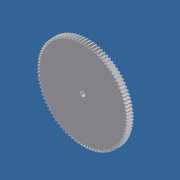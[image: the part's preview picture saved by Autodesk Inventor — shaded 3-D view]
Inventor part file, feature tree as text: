
AUTODESK INVENTOR PART (.ipt)
format: ipt  version: unknown  size: 956,928 bytes
history: native  units: in
note: dims shown in document units (in); Inventor stores cm internally (conversion verified against a paired STEP export)
features: extrude x3, sketch x3, imported_body x1
ambient origin geometry x8: Origin, YZ Plane, XZ Plane, XY Plane, X Axis, Y Axis, Z Axis, Center Point
bodies: Solid1 (feature_tree)
feature tree (7):
  imported_body  "Base1"
  extrude  "Extrusion2"  Depth=0.66in TaperAngle=0.0deg
  extrude  "Extrusion3"  Depth=0.41in TaperAngle=0.0deg
  extrude  "Extrusion4"  Depth=0.171in
  sketch  "Sketch2"  dims[d6=0.215in d7=0.66in d8=0.0in]
  sketch  "Sketch3"  dims[d9=0.7in d11=0.41in d12=0.0in]
  sketch  "Sketch4"  dims[d13=0.15in d14=0.171in d15=0.3in d16=0.0in]
